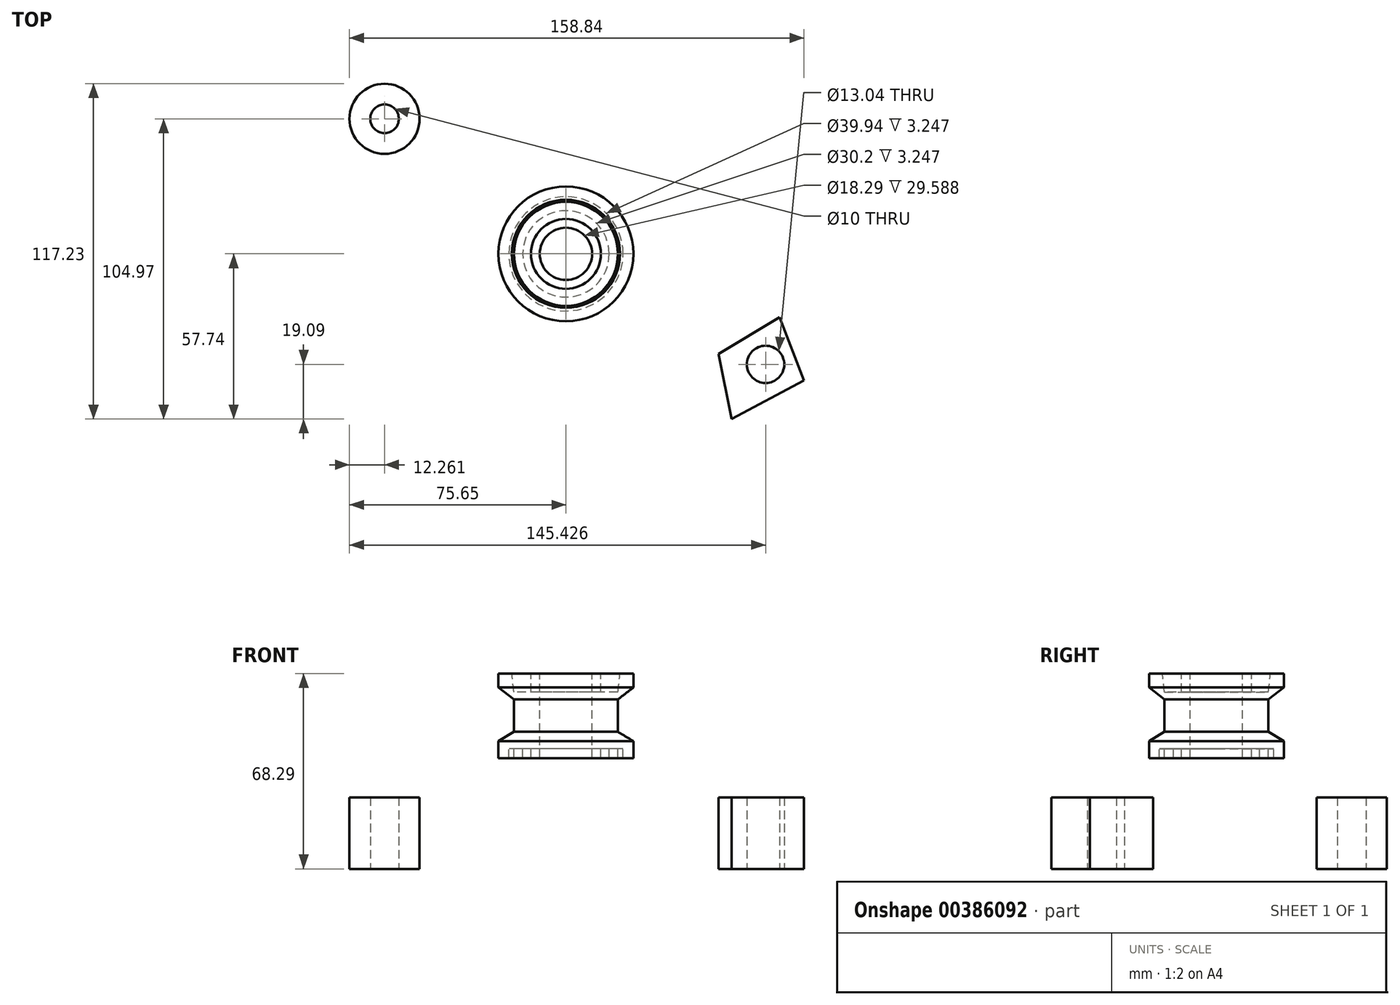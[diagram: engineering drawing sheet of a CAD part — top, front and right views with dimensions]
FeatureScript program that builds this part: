
annotation { "Feature Type Name" : "Feature", "Feature Type Description" : "" }
export const myFeature = defineFeature(function(context is Context, id is Id, definition is map)
    precondition{}
    {
        {
            var Q0;
            Q0=qCreatedBy(makeId("Top.planeOp"),FACE);
            var sketch = newSketch(context, id + "F0", { "sketchPlane" : qUnion([Q0])});
            skCircle(sketch, "E0", {"center": v(-63.39, 47.23) * mm, "radius": 12.26 * mm});
            skSolve(sketch);
        }
        {
            var Q0;
            Q0=makeQuery(id+"F0.imprint","IMPRINT",FACE,{"disambiguationData":[TD([[makeQuery(id+"F0.imprint","IMPRINT",EDGE,{"derivedFrom":sQuery(id+"F0.wireOp",EDGE,"E0")}),1.0]])]});
            extrude(context, id + "F1", {"entities" : qUnion([Q0]), "depth" : 25 * mm});
        }
        {
            var Q0;
            Q0=qCreatedBy(makeId("Front.planeOp"),FACE);
            var sketch = newSketch(context, id + "F2", { "sketchPlane" : qUnion([Q0])});
            skLineSegment(sketch, "E1", {"start": v(-18.89, 68.29) * mm, "end": v(-23.58, 68.29) * mm});
            skLineSegment(sketch, "E2", {"start": v(-23.58, 68.29) * mm, "end": v(-23.58, 63.41) * mm});
            skLineSegment(sketch, "E3", {"start": v(-23.58, 63.41) * mm, "end": v(-18.17, 59.27) * mm});
            skLineSegment(sketch, "E4", {"start": v(-18.17, 59.27) * mm, "end": v(-18.17, 47.9) * mm});
            skLineSegment(sketch, "E5", {"start": v(-18.17, 47.9) * mm, "end": v(-23.58, 44.65) * mm});
            skLineSegment(sketch, "E6", {"start": v(-23.58, 44.65) * mm, "end": v(-23.58, 38.7) * mm});
            skLineSegment(sketch, "E7", {"start": v(-23.58, 38.7) * mm, "end": v(-19.97, 38.7) * mm});
            skLineSegment(sketch, "E8", {"start": v(-19.97, 38.7) * mm, "end": v(-19.97, 41.95) * mm});
            skLineSegment(sketch, "E9", {"start": v(-19.97, 41.95) * mm, "end": v(-18.17, 41.95) * mm});
            skLineSegment(sketch, "E10", {"start": v(-18.17, 41.95) * mm, "end": v(-18.17, 38.7) * mm});
            skLineSegment(sketch, "E11", {"start": v(-18.17, 38.7) * mm, "end": v(-15.1, 38.7) * mm});
            skLineSegment(sketch, "E12", {"start": v(-15.1, 38.7) * mm, "end": v(-15.1, 41.95) * mm});
            skLineSegment(sketch, "E13", {"start": v(-15.1, 41.95) * mm, "end": v(-12.21, 41.95) * mm});
            skLineSegment(sketch, "E14", {"start": v(-12.21, 41.95) * mm, "end": v(-12.21, 38.7) * mm});
            skLineSegment(sketch, "E15", {"start": v(-12.21, 38.7) * mm, "end": v(-9.15, 38.7) * mm});
            skLineSegment(sketch, "E16", {"start": v(-9.15, 38.7) * mm, "end": v(-9.15, 68.29) * mm});
            skLineSegment(sketch, "E17", {"start": v(-9.15, 68.29) * mm, "end": v(-12.21, 68.29) * mm});
            skLineSegment(sketch, "E18", {"start": v(-12.21, 68.29) * mm, "end": v(-12.21, 61.8) * mm});
            skLineSegment(sketch, "E19", {"start": v(-12.21, 61.8) * mm, "end": v(-18.17, 61.8) * mm});
            skLineSegment(sketch, "E20", {"start": v(-18.17, 61.8) * mm, "end": v(-18.89, 68.29) * mm});
            skLineSegment(sketch, "E21", {"start": v(0, 73.52) * mm, "end": v(0, 32.74) * mm, "construction": true});
            skSolve(sketch);
        }
        {
            var Q0;
            Q0=makeQuery(id+"F2.imprint","IMPRINT",FACE,{"disambiguationData":[TD([[makeQuery(id+"F2.imprint","IMPRINT",EDGE,{"derivedFrom":sQuery(id+"F2.wireOp",EDGE,"E1")}),1.0]])]});
            var Q1;
            Q1=sQuery(id+"F2.wireOp",EDGE,"E21");
            revolve(context, id + "F3", {"entities" : qUnion([Q0]), "axis" : qUnion([Q1]), "revolveType" : RevolveType.FULL});
        }
        {
            var Q0;
            Q0=makeQuery(id+"F1.opExtrude","CAP_FACE",FACE,{"disambiguationData":[OSD([sQuery(id+"F0.wireOp",EDGE,"E0")])],"isStart":true});
            var sketch = newSketch(context, id + "F4", { "sketchPlane" : qUnion([Q0])});
            skCircle(sketch, "E22", {"center": v(-63.39, -47.23) * mm, "radius": 5 * mm});
            skSolve(sketch);
        }
        {
            var Q0;
            Q0=makeQuery(id+"F4.imprint","IMPRINT",FACE,{"disambiguationData":[TD([[makeQuery(id+"F4.imprint","IMPRINT",EDGE,{"derivedFrom":sQuery(id+"F4.wireOp",EDGE,"E22")}),1.0]])]});
            var Q1;
            Q1=makeQuery(id+"F1.opExtrude","CAP_FACE",FACE,{"disambiguationData":[OSD([sQuery(id+"F0.wireOp",EDGE,"E0")])],"isStart":false});
            extrude(context, id + "F5", {"entities" : qUnion([Q0]), "operationType" : NewBodyOperationType.REMOVE, "endBound" : BoundingType.UP_TO_SURFACE, "oppositeDirection" : true, "endBoundEntityFace" : qUnion([Q1]), "depth" : 187.7 * mm});
        }
        {
            var Q0;
            Q0=qCreatedBy(makeId("Top.planeOp"),FACE);
            var sketch = newSketch(context, id + "F6", { "sketchPlane" : qUnion([Q0])});
            skLineSegment(sketch, "E23", {"start": v(74.6, -22.12) * mm, "end": v(53.36, -35) * mm});
            skLineSegment(sketch, "E24", {"start": v(53.36, -35) * mm, "end": v(57.87, -57.74) * mm});
            skLineSegment(sketch, "E25", {"start": v(57.87, -57.74) * mm, "end": v(83.19, -44.22) * mm});
            skLineSegment(sketch, "E26", {"start": v(83.19, -44.22) * mm, "end": v(74.6, -22.12) * mm});
            skCircle(sketch, "E27", {"center": v(69.78, -38.65) * mm, "radius": 6.52 * mm});
            skSolve(sketch);
        }
        {
            var Q0;
            Q0=makeQuery(id+"F6.imprint","IMPRINT",FACE,{"disambiguationData":[TD([[makeQuery(id+"F6.imprint","IMPRINT",EDGE,{"derivedFrom":sQuery(id+"F6.wireOp",EDGE,"E23")}),1.0]])]});
            extrude(context, id + "F7", {"entities" : qUnion([Q0]), "depth" : 25 * mm});
        }
    });
